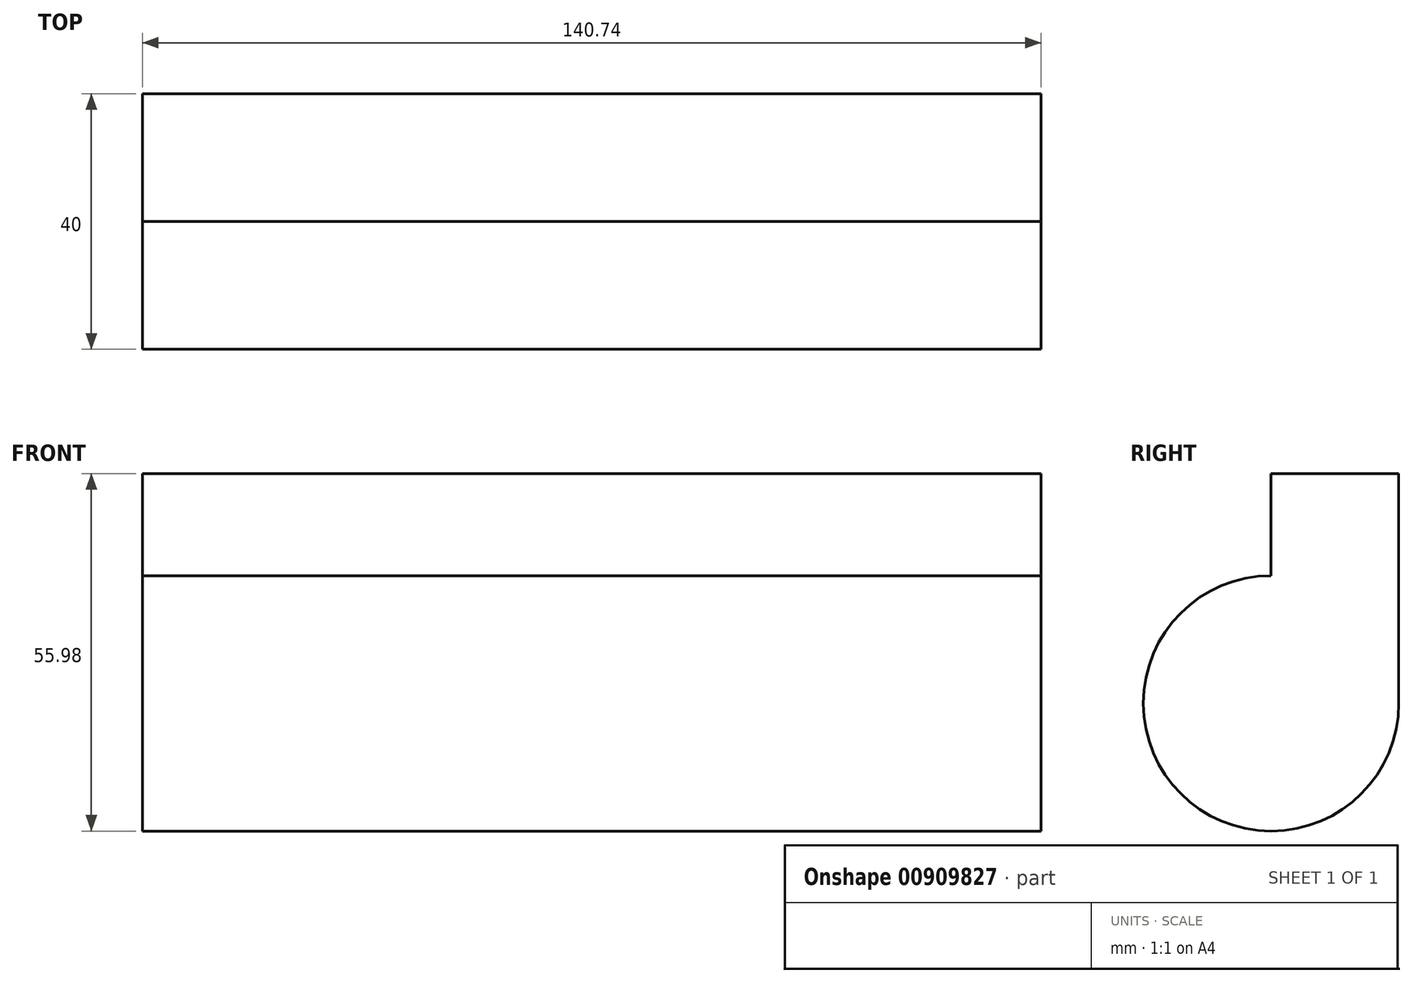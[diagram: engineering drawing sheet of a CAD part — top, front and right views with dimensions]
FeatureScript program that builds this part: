
annotation { "Feature Type Name" : "Feature", "Feature Type Description" : "" }
export const myFeature = defineFeature(function(context is Context, id is Id, definition is map)
    precondition{}
    {
        {
            var Q0;
            Q0=qCreatedBy(makeId("Front.planeOp"),FACE);
            var sketch = newSketch(context, id + "F0", { "sketchPlane" : qUnion([Q0])});
            skLineSegment(sketch, "E0.bottom", {"start": v(-70.37, 17.99) * mm, "end": v(70.37, 17.99) * mm});
            skLineSegment(sketch, "E0.top", {"start": v(-70.37, -17.99) * mm, "end": v(70.37, -17.99) * mm});
            skLineSegment(sketch, "E0.left", {"start": v(-70.37, 17.99) * mm, "end": v(-70.37, -17.99) * mm});
            skLineSegment(sketch, "E0.right", {"start": v(70.37, 17.99) * mm, "end": v(70.37, -17.99) * mm});
            skPoint(sketch, "E0.middle", {"position": v(0, 0) * mm});
            skSolve(sketch);
        }
        {
            var Q0;
            Q0 = qSketchRegion(id + "F0", true);
            extrude(context, id + "F1", {"entities" : qUnion([Q0]), "depth" : 20 * mm, "offsetDistance" : 25.4 * mm});
        }
        {
            var Q0;
            Q0=makeQuery(id+"F1.opExtrude","SWEPT_FACE",FACE,{"disambiguationData":[OSD([sQuery(id+"F0.wireOp",EDGE,"E0.top")])]});
            var Q1;
            Q1=makeQuery(id+"F1.opExtrude","CAP_EDGE",EDGE,{"disambiguationData":[OSD([sQuery(id+"F0.wireOp",EDGE,"E0.top")])],"isStart":false});
            revolve(context, id + "F2", {"operationType" : NewBodyOperationType.ADD, "surfaceOperationType" : NewSurfaceOperationType.NEW, "entities" : qUnion([Q0]), "axis" : qUnion([Q1]), "revolveType" : RevolveType.FULL});
        }
    });
